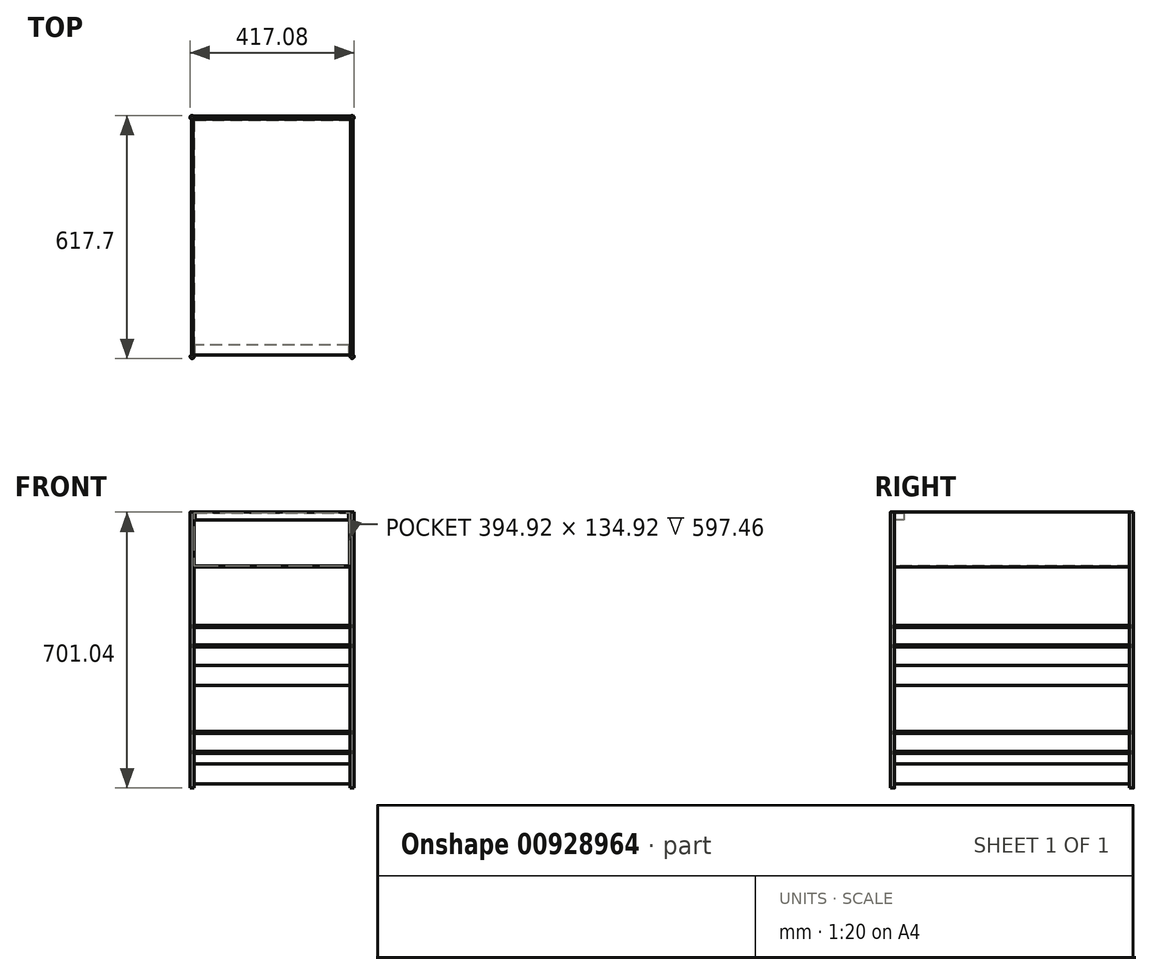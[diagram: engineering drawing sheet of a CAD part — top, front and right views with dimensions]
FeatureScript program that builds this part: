
annotation { "Feature Type Name" : "Feature", "Feature Type Description" : "" }
export const myFeature = defineFeature(function(context is Context, id is Id, definition is map)
    precondition{}
    {
        {
            var Q0;
            Q0=qCreatedBy(makeId("Front.planeOp"),FACE);
            var sketch = newSketch(context, id + "F0", { "sketchPlane" : qUnion([Q0])});
            skLineSegment(sketch, "E0.bottom", {"start": v(-200, 415) * mm, "end": v(200, 415) * mm});
            skLineSegment(sketch, "E0.top", {"start": v(-200, 275) * mm, "end": v(200, 275) * mm});
            skLineSegment(sketch, "E0.left", {"start": v(-200, 415) * mm, "end": v(-200, 275) * mm});
            skLineSegment(sketch, "E0.right", {"start": v(200, 415) * mm, "end": v(200, 275) * mm});
            skLineSegment(sketch, "E1", {"start": v(0, 345.05) * mm, "end": v(0, -353.85) * mm, "construction": true});
            skLineSegment(sketch, "E2", {"start": v(-302.56, 0) * mm, "end": v(343.59, 0) * mm, "construction": true});
            skLineSegment(sketch, "E3", {"start": v(-244.35, 345) * mm, "end": v(255.17, 345) * mm, "construction": true});
            skPoint(sketch, "E3.startSnap0", {"position": v(-200, 345) * mm});
            skLineSegment(sketch, "E4.bottom", {"start": v(-200, 25) * mm, "end": v(200, 25) * mm});
            skLineSegment(sketch, "E4.top", {"start": v(-200, -25) * mm, "end": v(200, -25) * mm});
            skLineSegment(sketch, "E4.left", {"start": v(-200, 25) * mm, "end": v(-200, -25) * mm});
            skLineSegment(sketch, "E4.right", {"start": v(200, 25) * mm, "end": v(200, -25) * mm});
            skLineSegment(sketch, "E5.bottom", {"start": v(-200, -225) * mm, "end": v(200, -225) * mm});
            skLineSegment(sketch, "E5.top", {"start": v(-200, -275) * mm, "end": v(200, -275) * mm});
            skLineSegment(sketch, "E5.left", {"start": v(-200, -225) * mm, "end": v(-200, -275) * mm});
            skLineSegment(sketch, "E5.right", {"start": v(200, -225) * mm, "end": v(200, -275) * mm});
            skSolve(sketch);
        }
        {
            var Q0;
            Q0 = qSketchRegion(id + "F0", true);
            extrude(context, id + "F1", {"entities" : qUnion([Q0]), "oppositeDirection" : true, "depth" : 600 * mm, "offsetDistance" : 25.4 * mm});
        }
        {
            var Q0;
            Q0=makeQuery(id+"F1.opExtrude","SWEPT_FACE",FACE,{"disambiguationData":[OSD([sQuery(id+"F0.wireOp",EDGE,"E0.bottom")])]});
            var sketch = newSketch(context, id + "F2", { "sketchPlane" : qUnion([Q0])});
            skCircle(sketch, "E6", {"center": v(203.54, -3.54) * mm, "radius": 5 * mm});
            skCircle(sketch, "E7", {"center": v(203.54, 603.54) * mm, "radius": 5 * mm});
            skCircle(sketch, "E8", {"center": v(-203.54, 603.54) * mm, "radius": 5 * mm});
            skCircle(sketch, "E9", {"center": v(-202.78, -4.16) * mm, "radius": 5 * mm});
            skSolve(sketch);
        }
        {
            var Q0;
            Q0 = qSketchRegion(id + "F2", true);
            extrude(context, id + "F3", {"entities" : qUnion([Q0]), "oppositeDirection" : true, "depth" : 701.04 * mm, "offsetDistance" : 25.4 * mm});
        }
        {
            var Q0;
            Q0=makeQuery(id+"F1.opExtrude","CAP_FACE",FACE,{"disambiguationData":[OSD([sQuery(id+"F0.wireOp",EDGE,"E0.bottom"),sQuery(id+"F0.wireOp",EDGE,"E0.top"),sQuery(id+"F0.wireOp",EDGE,"E0.left"),sQuery(id+"F0.wireOp",EDGE,"E0.right")])],"isStart":true});
            var sketch = newSketch(context, id + "F4", { "sketchPlane" : qUnion([Q0])});
            skLineSegment(sketch, "E10", {"start": v(-195, 415) * mm, "end": v(-195, 395) * mm});
            skLineSegment(sketch, "E11", {"start": v(-195, 395) * mm, "end": v(195, 395) * mm});
            skLineSegment(sketch, "E12", {"start": v(195, 395) * mm, "end": v(195, 415) * mm});
            skLineSegment(sketch, "E13", {"start": v(-195, 415) * mm, "end": v(195, 415) * mm});
            skSolve(sketch);
        }
        {
            var Q0;
            Q0=makeQuery(id+"F1.opExtrude","CAP_FACE",FACE,{"disambiguationData":[OSD([sQuery(id+"F0.wireOp",EDGE,"E0.bottom"),sQuery(id+"F0.wireOp",EDGE,"E0.top"),sQuery(id+"F0.wireOp",EDGE,"E0.left"),sQuery(id+"F0.wireOp",EDGE,"E0.right")])],"isStart":true});
            shell(context, id + "F5", {"entities" : qUnion([Q0]), "thickness" : 2.54 * mm});
        }
        {
            var Q0;
            Q0 = qSketchRegion(id + "F4", true);
            extrude(context, id + "F6", {"entities" : qUnion([Q0]), "operationType" : NewBodyOperationType.ADD, "oppositeDirection" : true, "depth" : 25.4 * mm, "offsetDistance" : 25.4 * mm});
        }
        {
            var Q0;
            Q0=makeQuery(id+"F3.opExtrude","SWEPT_FACE",FACE,{"disambiguationData":[OSD([sQuery(id+"F2.wireOp",EDGE,"E8")])]});
            cPlane(context, id + "F7", {"entities" : qUnion([Q0]), "cplaneType" : CPlaneType.LINE_ANGLE, "offset" : 25.4 * mm, "angle" : 90 * degree, "width" : 152.4 * mm, "height" : 152.4 * mm});
        }
        {
            var Q0;
            Q0=qCreatedBy(id+"F7.planeOp",FACE);
            var sketch = newSketch(context, id + "F8", { "sketchPlane" : qUnion([Q0])});
            skCircle(sketch, "E14", {"center": v(202.33, 125) * mm, "radius": 2.5 * mm});
            skCircle(sketch, "E15", {"center": v(202.33, 75) * mm, "radius": 2.5 * mm});
            skCircle(sketch, "E16", {"center": v(-203.3, 125) * mm, "radius": 2.5 * mm});
            skCircle(sketch, "E17", {"center": v(-203.3, 75) * mm, "radius": 2.5 * mm});
            skCircle(sketch, "E18", {"center": v(202.33, -145) * mm, "radius": 2.5 * mm});
            skCircle(sketch, "E19", {"center": v(202.33, -195) * mm, "radius": 2.5 * mm});
            skCircle(sketch, "E20", {"center": v(-202.97, -145) * mm, "radius": 2.5 * mm});
            skCircle(sketch, "E21", {"center": v(-202.97, -195) * mm, "radius": 2.5 * mm});
            skSolve(sketch);
        }
        {
            var Q0;
            Q0 = qSketchRegion(id + "F8", true);
            extrude(context, id + "F9", {"entities" : qUnion([Q0]), "oppositeDirection" : true, "depth" : 607.82 * mm, "offsetDistance" : 25.4 * mm});
        }
        {
            var Q0;
            Q0=makeQuery(id+"F3.opExtrude","SWEPT_FACE",FACE,{"disambiguationData":[OSD([sQuery(id+"F2.wireOp",EDGE,"E8")])]});
            cPlane(context, id + "F10", {"entities" : qUnion([Q0]), "cplaneType" : CPlaneType.LINE_ANGLE, "offset" : 25.4 * mm, "angle" : 0 * degree, "width" : 152.4 * mm, "height" : 152.4 * mm});
        }
        {
            var Q0;
            Q0=qCreatedBy(id+"F10.planeOp",FACE);
            var sketch = newSketch(context, id + "F11", { "sketchPlane" : qUnion([Q0])});
            skCircle(sketch, "E22", {"center": v(604.15, 124.58) * mm, "radius": 2.5 * mm});
            skCircle(sketch, "E23", {"center": v(604.15, 75.24) * mm, "radius": 2.5 * mm});
            skCircle(sketch, "E24", {"center": v(604.1, -145.03) * mm, "radius": 2.5 * mm});
            skCircle(sketch, "E25", {"center": v(603.98, -195.23) * mm, "radius": 2.5 * mm});
            skSolve(sketch);
        }
        {
            var Q0;
            Q0 = qSketchRegion(id + "F11", true);
            extrude(context, id + "F12", {"entities" : qUnion([Q0]), "depth" : 407.16 * mm, "offsetDistance" : 25.4 * mm});
        }
    });
